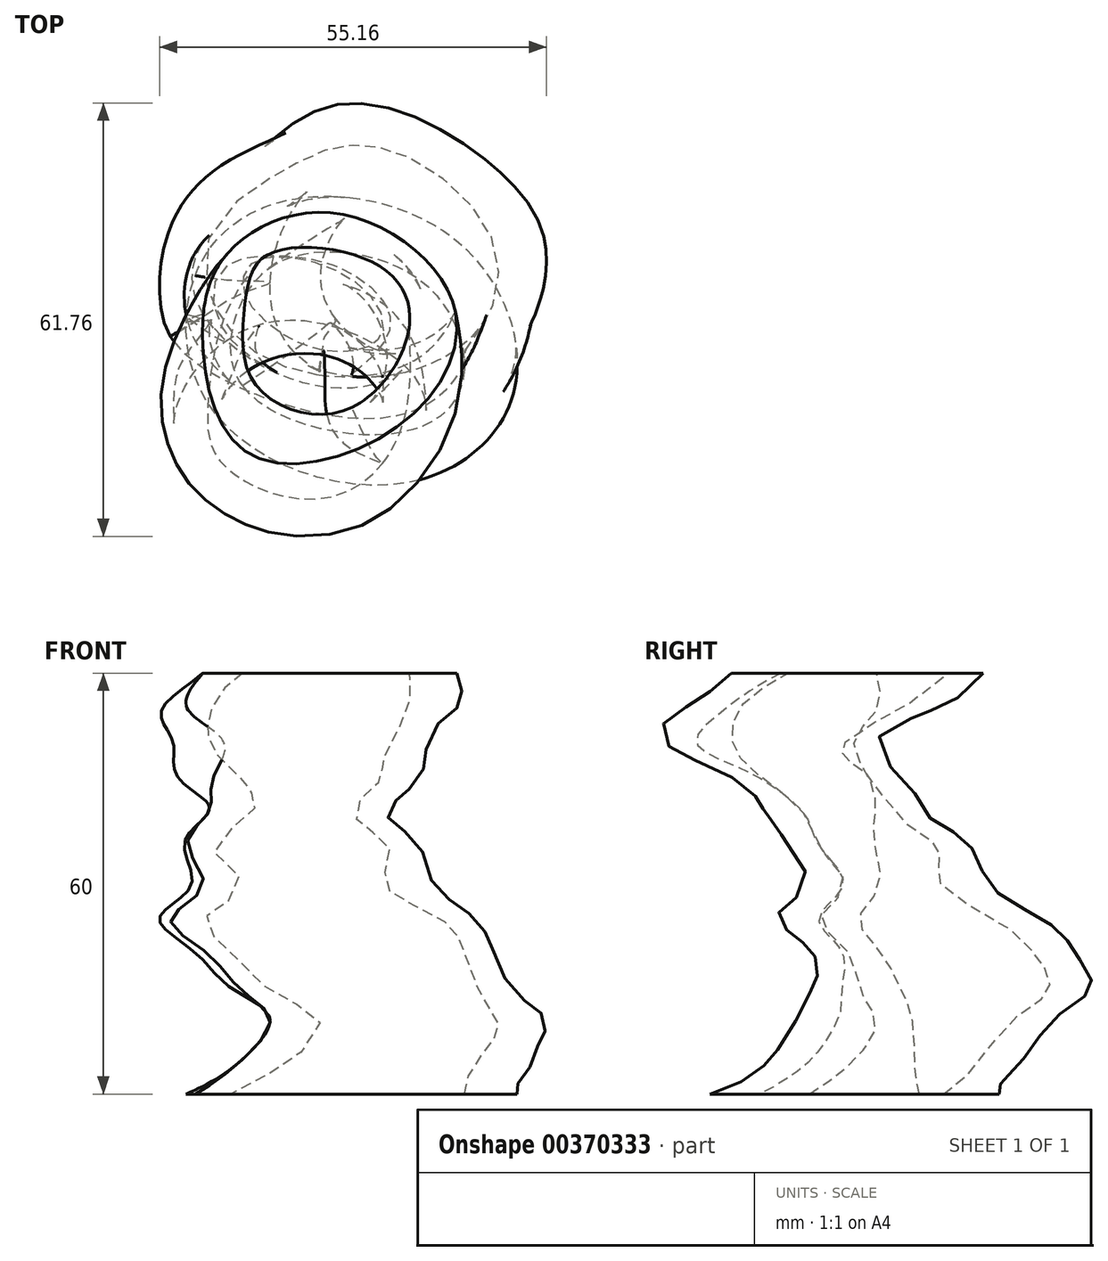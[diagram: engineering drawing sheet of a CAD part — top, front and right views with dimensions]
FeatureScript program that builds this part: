
annotation { "Feature Type Name" : "Feature", "Feature Type Description" : "" }
export const myFeature = defineFeature(function(context is Context, id is Id, definition is map)
    precondition{}
    {
        {
            var Q0;
            Q0=qCreatedBy(makeId("Top.planeOp"),FACE);
            var Q1;
            Q1 = qBodyType(qCreatedBy(id + "F1" ,EDGE), BodyType.WIRE);
            cPlane(context, id + "F0", {"entities" : qUnion([Q0, Q1]), "cplaneType" : CPlaneType.OFFSET, "offset" : 5 * mm, "width" : 152.4 * mm, "height" : 152.4 * mm});
        }
        {
            var Q0;
            Q0=qCreatedBy(id+"F0.planeOp",FACE);
            var sketch = newSketch(context, id + "F1", { "sketchPlane" : qUnion([Q0])});
            skFitSpline(sketch, "E0", {"points": [v(-22.58, 6.98) * mm, v(-9.58, 17.7) * mm, v(14.78, 11.86) * mm, v(22.9, -9.26) * mm, v(7.3, -22.58) * mm, v(-19.33, -13.16) * mm, v(-22.58, 6.98) * mm]});
            skSolve(sketch);
        }
        {
            var Q0;
            Q0=qCreatedBy(id+"F0.planeOp",FACE);
            var sketch = newSketch(context, id + "F2", { "sketchPlane" : qUnion([Q0])});
            skFitSpline(sketch, "E1", {"points": [v(-15.83, -8.7) * mm, v(-15.2, 4.5) * mm, v(-6.6, 10.17) * mm, v(9.96, 5.98) * mm, v(15.62, -7.65) * mm, v(6.6, -15.41) * mm, v(-15.83, -8.7) * mm]});
            skSolve(sketch);
        }
        {
            var Q0;
            Q0=qCreatedBy(id+"F0.planeOp",FACE);
            cPlane(context, id + "F3", {"entities" : qUnion([Q0]), "cplaneType" : CPlaneType.OFFSET, "offset" : 5 * mm, "width" : 152.4 * mm, "height" : 152.4 * mm});
        }
        {
            var Q0;
            Q0=qCreatedBy(id+"F3.planeOp",FACE);
            var sketch = newSketch(context, id + "F4", { "sketchPlane" : qUnion([Q0])});
            skFitSpline(sketch, "E2", {"points": [v(-15.41, 8.07) * mm, v(-7.45, 18.14) * mm, v(9.96, 21.5) * mm, v(24.43, 10.8) * mm, v(18.35, -11.43) * mm, v(-9.75, -8.5) * mm, v(-15.41, 8.07) * mm]});
            skSolve(sketch);
        }
        {
            var Q0;
            Q0=qCreatedBy(id+"F3.planeOp",FACE);
            var sketch = newSketch(context, id + "F5", { "sketchPlane" : qUnion([Q0])});
            skFitSpline(sketch, "E3", {"points": [v(-3.88, 13.53) * mm, v(-8.7, 6.19) * mm, v(-3.88, -4.93) * mm, v(13.32, -6.6) * mm, v(17.1, 8.28) * mm, v(8.07, 15.62) * mm, v(-3.88, 13.53) * mm]});
            skSolve(sketch);
        }
        {
            var Q0;
            Q0=qCreatedBy(id+"F3.planeOp",FACE);
            cPlane(context, id + "F6", {"entities" : qUnion([Q0]), "cplaneType" : CPlaneType.OFFSET, "offset" : 5 * mm, "width" : 152.4 * mm, "height" : 152.4 * mm});
        }
        {
            var Q0;
            Q0=qCreatedBy(id+"F6.planeOp",FACE);
            var sketch = newSketch(context, id + "F7", { "sketchPlane" : qUnion([Q0])});
            skFitSpline(sketch, "E4", {"points": [v(-9.75, 14.37) * mm, v(-9.96, -2.41) * mm, v(5.56, -10.8) * mm, v(20.87, -5.77) * mm, v(26.53, 14.16) * mm, v(5.14, 25.48) * mm, v(-9.75, 14.37) * mm]});
            skSolve(sketch);
        }
        {
            var Q0;
            Q0=qCreatedBy(id+"F6.planeOp",FACE);
            var sketch = newSketch(context, id + "F8", { "sketchPlane" : qUnion([Q0])});
            skFitSpline(sketch, "E5", {"points": [v(-3.46, 12.48) * mm, v(-3.88, 3.04) * mm, v(7.45, -4.93) * mm, v(19.6, 2.62) * mm, v(17.3, 15.83) * mm, v(3.04, 18.98) * mm, v(-3.46, 12.48) * mm]});
            skSolve(sketch);
        }
        {
            var Q0;
            Q0=qCreatedBy(id+"F6.planeOp",FACE);
            cPlane(context, id + "F9", {"entities" : qUnion([Q0]), "cplaneType" : CPlaneType.OFFSET, "offset" : 5 * mm, "width" : 152.4 * mm, "height" : 152.4 * mm});
        }
        {
            var Q0;
            Q0=qCreatedBy(id+"F9.planeOp",FACE);
            var sketch = newSketch(context, id + "F10", { "sketchPlane" : qUnion([Q0])});
            skFitSpline(sketch, "E6", {"points": [v(-15, 18.56) * mm, v(0, 31.41) * mm, v(20.45, 17.51) * mm, v(17.93, -3.67) * mm, v(-3.67, -7.03) * mm, v(-16.46, 4.93) * mm, v(-15, 18.56) * mm]});
            skSolve(sketch);
        }
        {
            var Q0;
            Q0=qCreatedBy(id+"F9.planeOp",FACE);
            var sketch = newSketch(context, id + "F11", { "sketchPlane" : qUnion([Q0])});
            skFitSpline(sketch, "E7", {"points": [v(-10.74, 16.58) * mm, v(-10.38, 4.86) * mm, v(4.43, -4.15) * mm, v(17.36, 4.43) * mm, v(11.86, 20.16) * mm, v(0, 25.3) * mm, v(-10.74, 16.58) * mm]});
            skSolve(sketch);
        }
        {
            var Q0;
            Q0=qCreatedBy(id+"F9.planeOp",FACE);
            cPlane(context, id + "F12", {"entities" : qUnion([Q0]), "cplaneType" : CPlaneType.OFFSET, "offset" : 5 * mm, "width" : 152.4 * mm, "height" : 152.4 * mm});
        }
        {
            var Q0;
            Q0=qCreatedBy(id+"F12.planeOp",FACE);
            var sketch = newSketch(context, id + "F13", { "sketchPlane" : qUnion([Q0])});
            skFitSpline(sketch, "E8", {"points": [v(-18.56, 19.4) * mm, v(-11.01, 26.53) * mm, v(0, 28.8) * mm, v(20.03, 7.03) * mm, v(4.72, -7.86) * mm, v(-21.08, 2.2) * mm, v(-18.56, 19.4) * mm]});
            skSolve(sketch);
        }
        {
            var Q0;
            Q0=qCreatedBy(id+"F12.planeOp",FACE);
            var sketch = newSketch(context, id + "F14", { "sketchPlane" : qUnion([Q0])});
            skFitSpline(sketch, "E9", {"points": [v(-9.62, 22.15) * mm, v(-17.26, 8.5) * mm, v(-7.03, -2.2) * mm, v(11.01, -1.78) * mm, v(15.46, 9.3) * mm, v(1.57, 21.5) * mm, v(-9.62, 22.15) * mm]});
            skSolve(sketch);
        }
        {
            var Q0;
            Q0=qCreatedBy(id+"F12.planeOp",FACE);
            cPlane(context, id + "F15", {"entities" : qUnion([Q0]), "cplaneType" : CPlaneType.OFFSET, "offset" : 5 * mm, "width" : 152.4 * mm, "height" : 152.4 * mm});
        }
        {
            var Q0;
            Q0=qCreatedBy(id+"F15.planeOp",FACE);
            var sketch = newSketch(context, id + "F16", { "sketchPlane" : qUnion([Q0])});
            skFitSpline(sketch, "E10", {"points": [v(-24.22, 17.3) * mm, v(-27.58, 3.46) * mm, v(-21.92, -5.77) * mm, v(9.96, -11.64) * mm, v(15.41, 11.43) * mm, v(-7.86, 24.43) * mm, v(-24.22, 17.3) * mm]});
            skSolve(sketch);
        }
        {
            var Q0;
            Q0=qCreatedBy(id+"F15.planeOp",FACE);
            var sketch = newSketch(context, id + "F17", { "sketchPlane" : qUnion([Q0])});
            skFitSpline(sketch, "E11", {"points": [v(-20.87, 11.01) * mm, v(-10.8, 17.51) * mm, v(9.33, 9.96) * mm, v(11.43, -1.78) * mm, v(1.78, -7.24) * mm, v(-15.62, -2.62) * mm, v(-20.87, 11.01) * mm]});
            skSolve(sketch);
        }
        {
            var Q0;
            Q0=qCreatedBy(id+"F15.planeOp",FACE);
            cPlane(context, id + "F18", {"entities" : qUnion([Q0]), "cplaneType" : CPlaneType.OFFSET, "offset" : 5 * mm, "width" : 152.4 * mm, "height" : 152.4 * mm});
        }
        {
            var Q0;
            Q0=qCreatedBy(id+"F18.planeOp",FACE);
            var sketch = newSketch(context, id + "F19", { "sketchPlane" : qUnion([Q0])});
            skFitSpline(sketch, "E12", {"points": [v(-20.03, 13.53) * mm, v(-7.03, 16.67) * mm, v(7.45, 9.12) * mm, v(10.6, -3.67) * mm, v(-4.3, -8.91) * mm, v(-22.34, 3.25) * mm, v(-20.03, 13.53) * mm]});
            skSolve(sketch);
        }
        {
            var Q0;
            Q0=qCreatedBy(id+"F18.planeOp",FACE);
            var sketch = newSketch(context, id + "F20", { "sketchPlane" : qUnion([Q0])});
            skFitSpline(sketch, "E13", {"points": [v(-14.79, 8.5) * mm, v(-7.65, 9.75) * mm, v(2.41, 4.3) * mm, v(3.88, -2) * mm, v(-5.14, -3.46) * mm, v(-15.2, 3.67) * mm, v(-14.79, 8.5) * mm]});
            skSolve(sketch);
        }
        {
            var Q0;
            Q0=qCreatedBy(id+"F18.planeOp",FACE);
            cPlane(context, id + "F21", {"entities" : qUnion([Q0]), "cplaneType" : CPlaneType.OFFSET, "offset" : 5 * mm, "width" : 152.4 * mm, "height" : 152.4 * mm});
        }
        {
            var Q0;
            Q0=qCreatedBy(id+"F21.planeOp",FACE);
            var sketch = newSketch(context, id + "F22", { "sketchPlane" : qUnion([Q0])});
            skFitSpline(sketch, "E14", {"points": [v(-22.13, 10.6) * mm, v(-21.7, -3.04) * mm, v(2.62, -9.96) * mm, v(8.7, 5.77) * mm, v(-6.19, 14.16) * mm, v(-14.79, 13.95) * mm, v(-22.13, 10.6) * mm]});
            skSolve(sketch);
        }
        {
            var Q0;
            Q0=qCreatedBy(id+"F21.planeOp",FACE);
            var sketch = newSketch(context, id + "F23", { "sketchPlane" : qUnion([Q0])});
            skFitSpline(sketch, "E15", {"points": [v(-18.77, 7.65) * mm, v(-18.77, 0) * mm, v(-3.46, -7.03) * mm, v(5.14, 0) * mm, v(-1.78, 7.86) * mm, v(-11.85, 9.54) * mm, v(-18.77, 7.65) * mm]});
            skSolve(sketch);
        }
        {
            var Q0;
            Q0=qCreatedBy(id+"F21.planeOp",FACE);
            cPlane(context, id + "F24", {"entities" : qUnion([Q0]), "cplaneType" : CPlaneType.OFFSET, "offset" : 5 * mm, "width" : 152.4 * mm, "height" : 152.4 * mm});
        }
        {
            var Q0;
            Q0=qCreatedBy(id+"F24.planeOp",FACE);
            var sketch = newSketch(context, id + "F25", { "sketchPlane" : qUnion([Q0])});
            skFitSpline(sketch, "E16", {"points": [v(-20.45, 2.83) * mm, v(-17.51, -8.7) * mm, v(-2.83, -14.58) * mm, v(4.72, -4.93) * mm, v(-2.62, 6.6) * mm, v(-16.46, 6.19) * mm, v(-20.45, 2.83) * mm]});
            skSolve(sketch);
        }
        {
            var Q0;
            Q0=qCreatedBy(id+"F24.planeOp",FACE);
            var sketch = newSketch(context, id + "F26", { "sketchPlane" : qUnion([Q0])});
            skFitSpline(sketch, "E17", {"points": [v(-14.37, 0) * mm, v(-12.69, -5.77) * mm, v(-2.83, -9.33) * mm, v(0, -5.35) * mm, v(-5.14, 2.2) * mm, v(-12.06, 2.41) * mm, v(-14.37, 0) * mm]});
            skSolve(sketch);
        }
        {
            var Q0;
            Q0=qCreatedBy(id+"F24.planeOp",FACE);
            cPlane(context, id + "F27", {"entities" : qUnion([Q0]), "cplaneType" : CPlaneType.OFFSET, "offset" : 5 * mm, "width" : 152.4 * mm, "height" : 152.4 * mm});
        }
        {
            var Q0;
            Q0=qCreatedBy(id+"F27.planeOp",FACE);
            var sketch = newSketch(context, id + "F28", { "sketchPlane" : qUnion([Q0])});
            skFitSpline(sketch, "E18", {"points": [v(-24.85, -8.07) * mm, v(-14.58, -18.14) * mm, v(6.19, -14.79) * mm, v(7.03, 0) * mm, v(-11.43, 4.3) * mm, v(-22.55, -2.62) * mm, v(-24.85, -8.07) * mm]});
            skSolve(sketch);
        }
        {
            var Q0;
            Q0=qCreatedBy(id+"F27.planeOp",FACE);
            var sketch = newSketch(context, id + "F29", { "sketchPlane" : qUnion([Q0])});
            skFitSpline(sketch, "E19", {"points": [v(-16.04, -6.82) * mm, v(-13.74, -13.53) * mm, v(0, -14.37) * mm, v(3.67, -6.4) * mm, v(-5.35, 0) * mm, v(-14.79, -2) * mm, v(-16.04, -6.82) * mm]});
            skSolve(sketch);
        }
        {
            var Q0;
            Q0=qCreatedBy(id+"F27.planeOp",FACE);
            cPlane(context, id + "F30", {"entities" : qUnion([Q0]), "cplaneType" : CPlaneType.OFFSET, "offset" : 5 * mm, "width" : 152.4 * mm, "height" : 152.4 * mm});
        }
        {
            var Q0;
            Q0=qCreatedBy(id+"F30.planeOp",FACE);
            var sketch = newSketch(context, id + "F31", { "sketchPlane" : qUnion([Q0])});
            skFitSpline(sketch, "E20", {"points": [v(-25.7, -14.79) * mm, v(-15.83, -27.37) * mm, v(2.62, -26.74) * mm, v(10.38, -12.9) * mm, v(5.14, -4.09) * mm, v(-13.74, 0) * mm, v(-25.7, -14.79) * mm]});
            skSolve(sketch);
        }
        {
            var Q0;
            Q0=qCreatedBy(id+"F30.planeOp",FACE);
            var sketch = newSketch(context, id + "F32", { "sketchPlane" : qUnion([Q0])});
            skFitSpline(sketch, "E21", {"points": [v(-18.98, -10.38) * mm, v(-19.4, -18.77) * mm, v(-3.04, -24.43) * mm, v(5.35, -13.74) * mm, v(-2, -4.72) * mm, v(-12.27, -4.72) * mm, v(-18.98, -10.38) * mm]});
            skSolve(sketch);
        }
        {
            var Q0;
            Q0=qCreatedBy(id+"F30.planeOp",FACE);
            cPlane(context, id + "F33", {"entities" : qUnion([Q0]), "cplaneType" : CPlaneType.OFFSET, "offset" : 5 * mm, "width" : 152.4 * mm, "height" : 152.4 * mm});
        }
        {
            var Q0;
            Q0=qCreatedBy(id+"F33.planeOp",FACE);
            var sketch = newSketch(context, id + "F34", { "sketchPlane" : qUnion([Q0])});
            skFitSpline(sketch, "E22", {"points": [v(-21.7, 3.67) * mm, v(-26.95, -12.69) * mm, v(-10.17, -26.32) * mm, v(13.32, -15.83) * mm, v(8.07, 4.93) * mm, v(-11.22, 9.12) * mm, v(-21.7, 3.67) * mm]});
            skSolve(sketch);
        }
        {
            var Q0;
            Q0=qCreatedBy(id+"F33.planeOp",FACE);
            var sketch = newSketch(context, id + "F35", { "sketchPlane" : qUnion([Q0])});
            skFitSpline(sketch, "E23", {"points": [v(-20.03, -5.35) * mm, v(-17.1, -16.88) * mm, v(3.88, -18.14) * mm, v(6.4, -3.67) * mm, v(-5.77, 4.3) * mm, v(-17.93, 0) * mm, v(-20.03, -5.35) * mm]});
            skSolve(sketch);
        }
        {
            var Q0;
            Q0=qCreatedBy(id+"F33.planeOp",FACE);
            cPlane(context, id + "F36", {"entities" : qUnion([Q0]), "cplaneType" : CPlaneType.OFFSET, "offset" : 5 * mm, "width" : 152.4 * mm, "height" : 152.4 * mm});
        }
        {
            var Q0;
            Q0=qCreatedBy(id+"F36.planeOp",FACE);
            var sketch = newSketch(context, id + "F37", { "sketchPlane" : qUnion([Q0])});
            skFitSpline(sketch, "E24", {"points": [v(-21.5, -2.41) * mm, v(-15, -18.35) * mm, v(6.19, -14.58) * mm, v(14.37, 2.41) * mm, v(-2.2, 15.83) * mm, v(-17.93, 10.17) * mm, v(-21.5, -2.41) * mm]});
            skSolve(sketch);
        }
        {
            var Q0;
            Q0=qCreatedBy(id+"F36.planeOp",FACE);
            var sketch = newSketch(context, id + "F38", { "sketchPlane" : qUnion([Q0])});
            skFitSpline(sketch, "E25", {"points": [v(-15.41, 3.46) * mm, v(-14.16, -8.28) * mm, v(-3.25, -12.69) * mm, v(5.56, -6.4) * mm, v(7.86, 2.62) * mm, v(1.78, 9.33) * mm, v(-12.27, 9.96) * mm, v(-15.41, 3.46) * mm]});
            skSolve(sketch);
        }
        {
            var Q0;
            Q0 = qSketchRegion(id + "F1", true);
            var Q1;
            Q1 = qSketchRegion(id + "F4", true);
            var Q2;
            Q2 = qSketchRegion(id + "F7", true);
            var Q3;
            Q3 = qSketchRegion(id + "F10", true);
            var Q4;
            Q4 = qSketchRegion(id + "F13", true);
            var Q5;
            Q5 = qSketchRegion(id + "F16", true);
            var Q6;
            Q6 = qSketchRegion(id + "F19", true);
            var Q7;
            Q7 = qSketchRegion(id + "F22", true);
            var Q8;
            Q8 = qSketchRegion(id + "F25", true);
            var Q9;
            Q9 = qSketchRegion(id + "F28", true);
            var Q10;
            Q10 = qSketchRegion(id + "F31", true);
            var Q11;
            Q11 = qSketchRegion(id + "F34", true);
            var Q12;
            Q12 = qSketchRegion(id + "F37", true);
            loft(context, id + "F39", {"sheetProfilesArray" : [{ "sheetProfileEntities" : qUnion([Q0]) }, { "sheetProfileEntities" : qUnion([Q1]) }, { "sheetProfileEntities" : qUnion([Q2]) }, { "sheetProfileEntities" : qUnion([Q3]) }, { "sheetProfileEntities" : qUnion([Q4]) }, { "sheetProfileEntities" : qUnion([Q5]) }, { "sheetProfileEntities" : qUnion([Q6]) }, { "sheetProfileEntities" : qUnion([Q7]) }, { "sheetProfileEntities" : qUnion([Q8]) }, { "sheetProfileEntities" : qUnion([Q9]) }, { "sheetProfileEntities" : qUnion([Q10]) }, { "sheetProfileEntities" : qUnion([Q11]) }, { "sheetProfileEntities" : qUnion([Q12]) }]});
        }
        {
            var Q1;
            Q1 = qSketchRegion(id + "F2", true);
            var Q2;
            Q2 = qSketchRegion(id + "F5", true);
            var Q3;
            Q3 = qSketchRegion(id + "F8", true);
            var Q4;
            Q4 = qSketchRegion(id + "F11", true);
            var Q5;
            Q5 = qSketchRegion(id + "F14", true);
            var Q6;
            Q6 = qSketchRegion(id + "F17", true);
            var Q7;
            Q7 = qSketchRegion(id + "F20", true);
            var Q8;
            Q8 = qSketchRegion(id + "F23", true);
            var Q9;
            Q9 = qSketchRegion(id + "F26", true);
            var Q10;
            Q10 = qSketchRegion(id + "F29", true);
            var Q11;
            Q11 = qSketchRegion(id + "F32", true);
            var Q12;
            Q12 = qSketchRegion(id + "F35", true);
            var Q13;
            Q13 = qSketchRegion(id + "F38", true);
            loft(context, id + "F40", {"operationType" : NewBodyOperationType.REMOVE, "sheetProfilesArray" : [{ "sheetProfileEntities" : qUnion([Q1]) }, { "sheetProfileEntities" : qUnion([Q2]) }, { "sheetProfileEntities" : qUnion([Q3]) }, { "sheetProfileEntities" : qUnion([Q4]) }, { "sheetProfileEntities" : qUnion([Q5]) }, { "sheetProfileEntities" : qUnion([Q6]) }, { "sheetProfileEntities" : qUnion([Q7]) }, { "sheetProfileEntities" : qUnion([Q8]) }, { "sheetProfileEntities" : qUnion([Q9]) }, { "sheetProfileEntities" : qUnion([Q10]) }, { "sheetProfileEntities" : qUnion([Q11]) }, { "sheetProfileEntities" : qUnion([Q12]) }, { "sheetProfileEntities" : qUnion([Q13]) }]});
        }
    });
